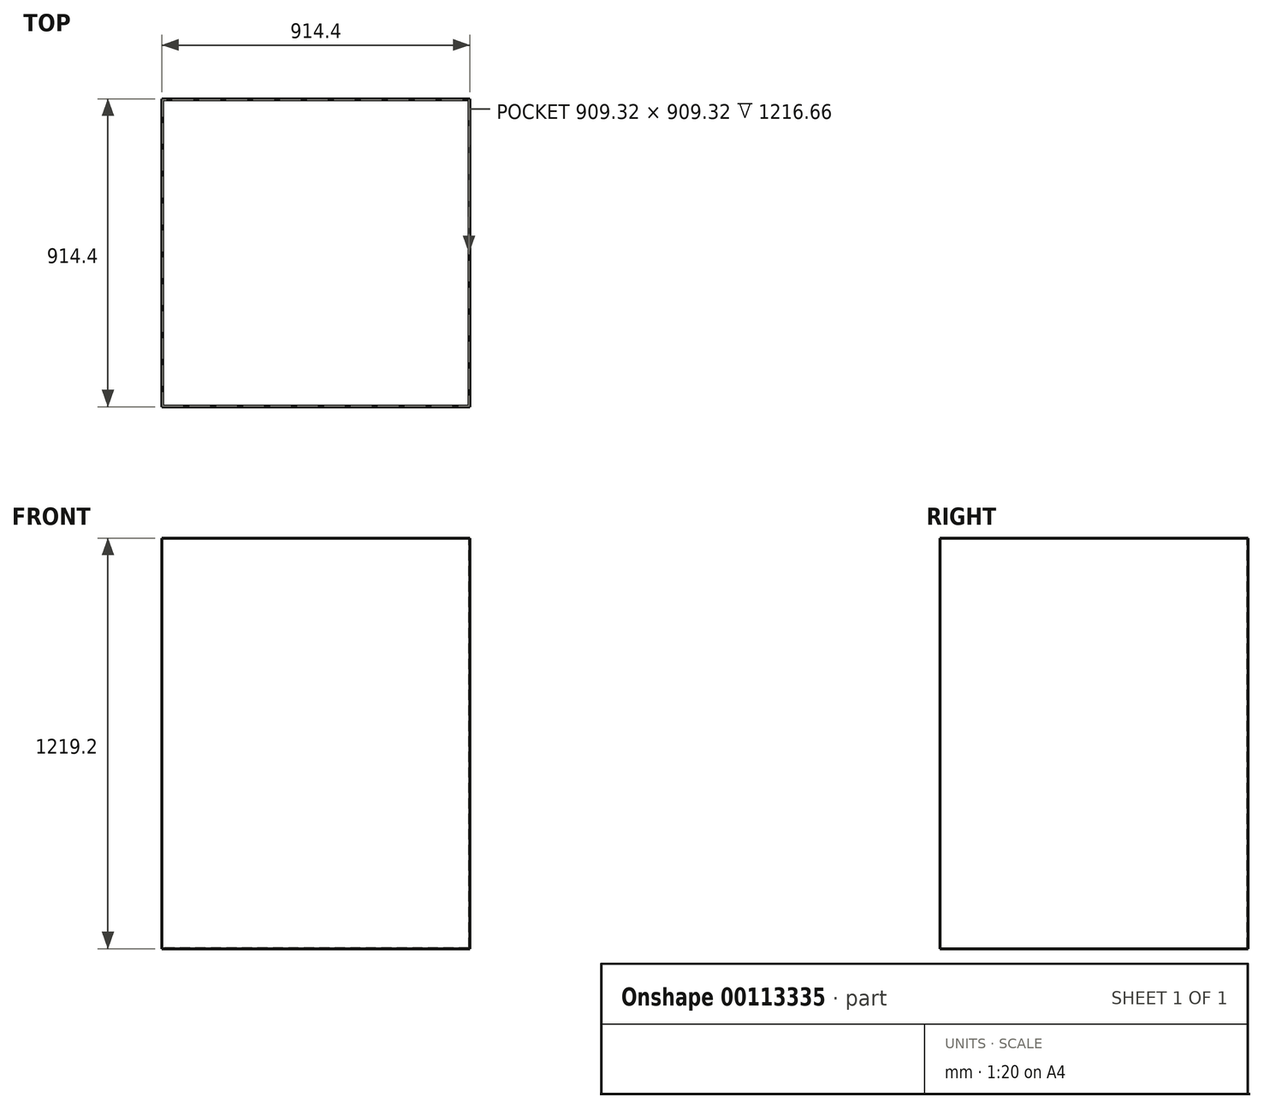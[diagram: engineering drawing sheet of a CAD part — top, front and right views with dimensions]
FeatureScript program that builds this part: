
annotation { "Feature Type Name" : "Feature", "Feature Type Description" : "" }
export const myFeature = defineFeature(function(context is Context, id is Id, definition is map)
    precondition{}
    {
        {
            var Q0;
            Q0=qCreatedBy(makeId("Front.planeOp"),FACE);
            var sketch = newSketch(context, id + "F0", { "sketchPlane" : qUnion([Q0])});
            skLineSegment(sketch, "E0.bottom", {"start": v(457.2, -609.6) * mm, "end": v(-457.2, -609.6) * mm});
            skLineSegment(sketch, "E0.top", {"start": v(457.2, 609.6) * mm, "end": v(-457.2, 609.6) * mm});
            skLineSegment(sketch, "E0.left", {"start": v(457.2, -609.6) * mm, "end": v(457.2, 609.6) * mm});
            skLineSegment(sketch, "E0.right", {"start": v(-457.2, -609.6) * mm, "end": v(-457.2, 609.6) * mm});
            skPoint(sketch, "E0.middle", {"position": v(0, 0) * mm});
            skSolve(sketch);
        }
        {
            var Q0;
            Q0 = qSketchRegion(id + "F0", true);
            extrude(context, id + "F1", {"entities" : qUnion([Q0]), "endBound" : BoundingType.SYMMETRIC, "depth" : 914.4 * mm});
        }
        {
            var Q0;
            Q0=makeQuery(id+"F1.opExtrude","SWEPT_FACE",FACE,{"disambiguationData":[OSD([sQuery(id+"F0.wireOp",EDGE,"E0.top")])]});
            shell(context, id + "F2", {"entities" : qUnion([Q0]), "thickness" : 2.54 * mm});
        }
    });
